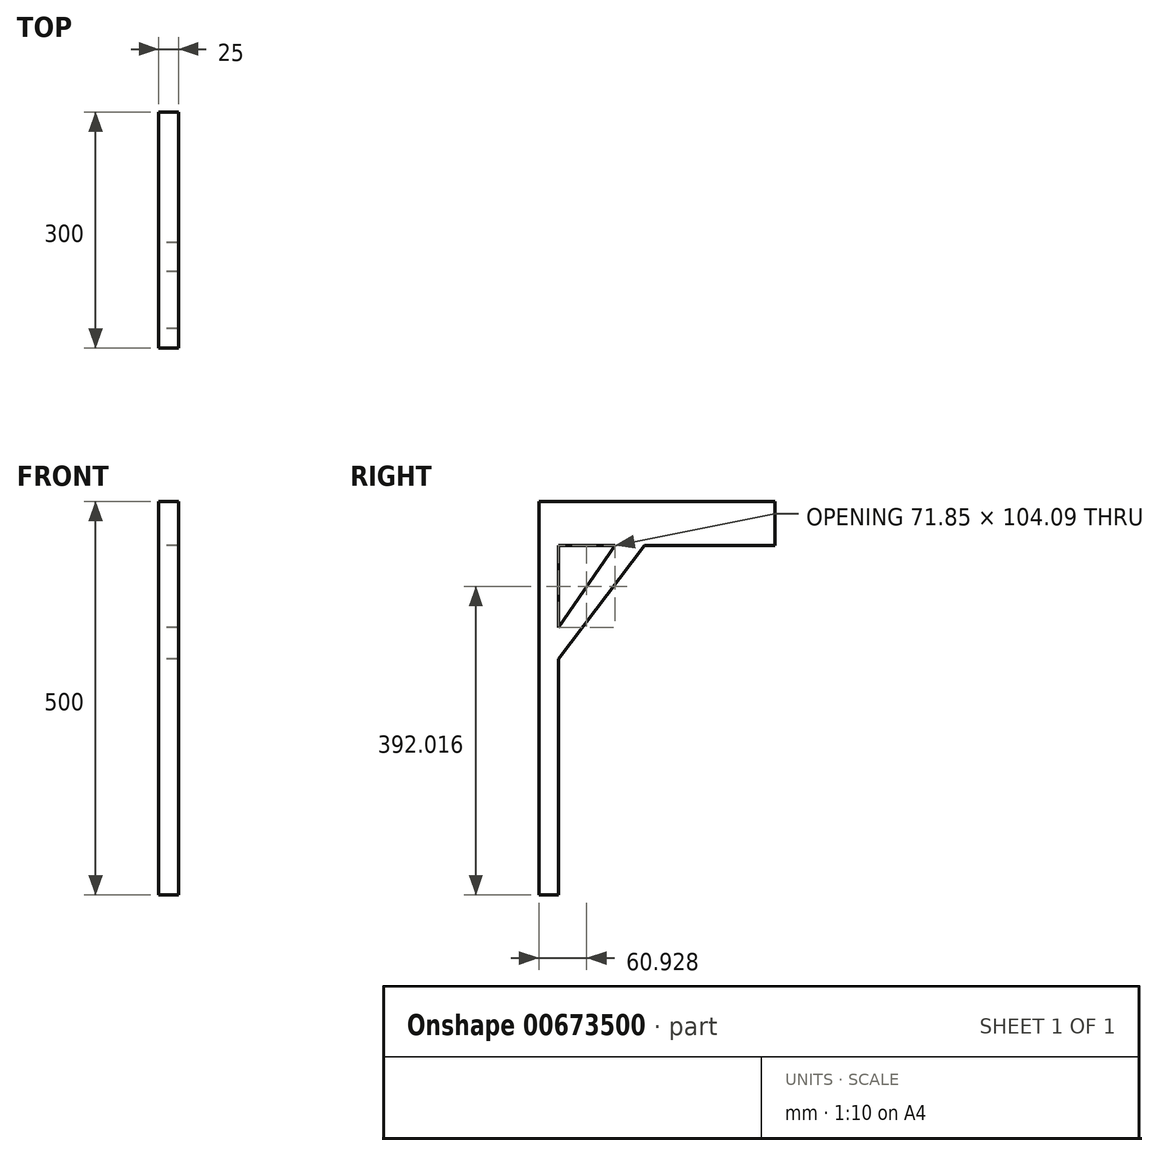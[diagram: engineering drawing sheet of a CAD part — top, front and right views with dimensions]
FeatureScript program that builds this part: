
annotation { "Feature Type Name" : "Feature", "Feature Type Description" : "" }
export const myFeature = defineFeature(function(context is Context, id is Id, definition is map)
    precondition{}
    {
        {
            var Q0;
            Q0=qCreatedBy(makeId("Right.planeOp"),FACE);
            var sketch = newSketch(context, id + "F0", { "sketchPlane" : qUnion([Q0])});
            skLineSegment(sketch, "E0.top", {"start": v(-76.9, -349.31) * mm, "end": v(-51.9, -349.31) * mm});
            skLineSegment(sketch, "E0.left", {"start": v(-76.9, 150.69) * mm, "end": v(-76.9, -349.31) * mm});
            skLineSegment(sketch, "E1", {"start": v(-51.9, -349.31) * mm, "end": v(-51.9, 94.75) * mm});
            skLineSegment(sketch, "E2", {"start": v(-51.9, 94.75) * mm, "end": v(223.1, 94.75) * mm});
            skLineSegment(sketch, "E3", {"start": v(223.1, 94.75) * mm, "end": v(223.1, 150.7) * mm});
            skLineSegment(sketch, "E4", {"start": v(-76.9, 150.69) * mm, "end": v(223.1, 150.7) * mm});
            skLineSegment(sketch, "E5", {"start": v(19.95, 94.75) * mm, "end": v(-51.9, -9.34) * mm});
            skLineSegment(sketch, "E6", {"start": v(-51.9, -9.34) * mm, "end": v(-51.9, -49.31) * mm});
            skLineSegment(sketch, "E7", {"start": v(-51.9, -49.31) * mm, "end": v(57.22, 94.75) * mm});
            skSolve(sketch);
        }
        {
            var Q0;
            {var subQ5=sQuery(id+"F0.wireOp",EDGE,"E0.top");Q0=makeQuery(id+"F0.imprint","IMPRINT",FACE,{"disambiguationData":[TD([[makeQuery(id+"F0.imprint","IMPRINT",EDGE,{"derivedFrom":subQ5}),1.0]])]});}
            var Q1;
            {var subQ0=sQuery(id+"F0.wireOp",EDGE,"E5");Q1=makeQuery(id+"F0.imprint","IMPRINT",FACE,{"disambiguationData":[TD([[makeQuery(id+"F0.imprint","IMPRINT",EDGE,{"derivedFrom":subQ0}),1.0]])]});}
            extrude(context, id + "F1", {"entities" : qUnion([Q0, Q1]), "depth" : 25 * mm, "offsetDistance" : 25 * mm});
        }
    });
